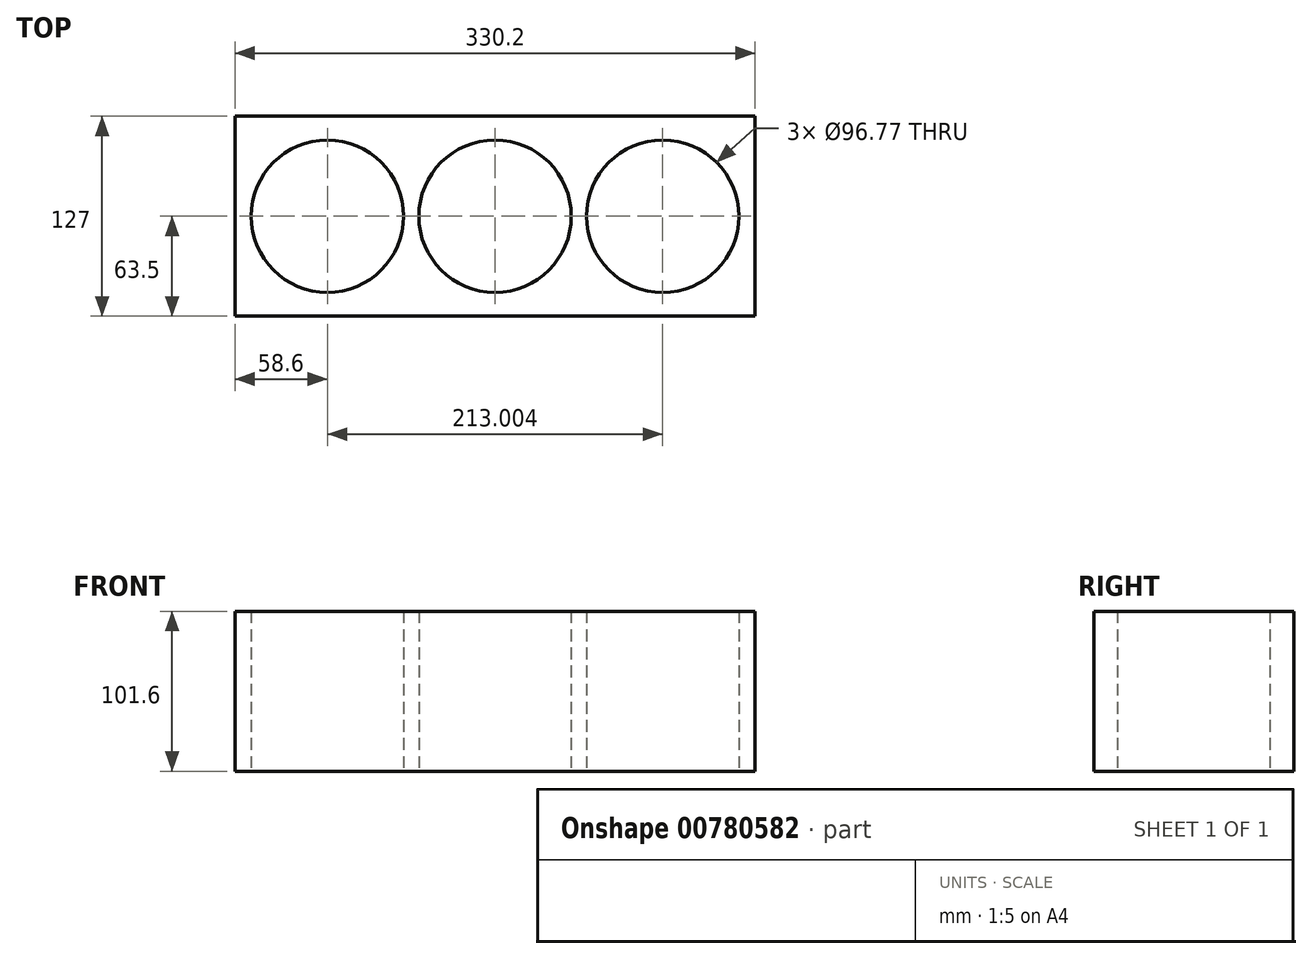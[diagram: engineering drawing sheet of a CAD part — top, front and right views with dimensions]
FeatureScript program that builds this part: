
annotation { "Feature Type Name" : "Feature", "Feature Type Description" : "" }
export const myFeature = defineFeature(function(context is Context, id is Id, definition is map)
    precondition{}
    {
        {
            var Q0;
            Q0=qCreatedBy(makeId("Top.planeOp"),FACE);
            var sketch = newSketch(context, id + "F0", { "sketchPlane" : qUnion([Q0])});
            skCircle(sketch, "E0", {"center": v(-157.9, 0) * mm, "radius": 48.39 * mm});
            skCircle(sketch, "E1.1.0.0", {"center": v(-51.4, 0) * mm, "radius": 48.39 * mm});
            skCircle(sketch, "E1.2.0.0", {"center": v(55.1, 0) * mm, "radius": 48.39 * mm});
            skLineSegment(sketch, "E1.direction1", {"start": v(-157.9, 0) * mm, "end": v(-51.4, 0) * mm, "construction": true});
            skLineSegment(sketch, "E2.bottom", {"start": v(113.7, -63.5) * mm, "end": v(-216.5, -63.5) * mm});
            skLineSegment(sketch, "E2.top", {"start": v(113.7, 63.5) * mm, "end": v(-216.5, 63.5) * mm});
            skLineSegment(sketch, "E2.left", {"start": v(113.7, -63.5) * mm, "end": v(113.7, 63.5) * mm});
            skLineSegment(sketch, "E2.right", {"start": v(-216.5, -63.5) * mm, "end": v(-216.5, 63.5) * mm});
            skSolve(sketch);
        }
        {
            var Q0;
            Q0=makeQuery(id+"F0.imprint","IMPRINT",FACE,{"disambiguationData":[TD([[makeQuery(id+"F0.imprint","IMPRINT",EDGE,{"derivedFrom":sQuery(id+"F0.wireOp",EDGE,"E0")}),-1.0]])]});
            extrude(context, id + "F1", {"entities" : qUnion([Q0]), "depth" : 101.6 * mm, "offsetDistance" : 25.4 * mm});
        }
    });
